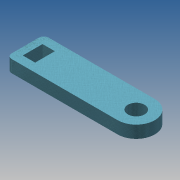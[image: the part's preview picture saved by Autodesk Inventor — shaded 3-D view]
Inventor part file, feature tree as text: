
AUTODESK INVENTOR PART (.ipt)
format: ipt  version: 2015 SP1 (Build 190203100, 203)  size: 132,608 bytes
history: native  units: mm
features: extrude x2, sketch x2, fillet x1, projected_geometry x1
ambient origin geometry x8: Origin, YZ Plane, XZ Plane, XY Plane, X Axis, Y Axis, Z Axis, Center Point
bodies: Volumenkörper1 (feature_tree)
feature tree (6):
  extrude  "Extrusion1"  Depth=3.5mm
  extrude  "Extrusion3"  Depth=2.0mm
  fillet  "Rundung1"  Radius=16.5mm
  sketch  "Skizze1"  dims[d0=3.5mm d1=15.5mm]
  sketch  "Skizze3"  dims[d2=15.5mm d3=22.0mm d4=16.5mm d5=11.0mm d6=6.8mm d7=15.0mm d10=15.0mm d11=45.0mm d12=5.0mm d13=0.0mm d17=5.0mm d18=8.0mm d19=3.0mm d20=5.0mm d21=0.0mm d22=2.0mm]
  projected_geometry  "Projizierte Kontur2"
